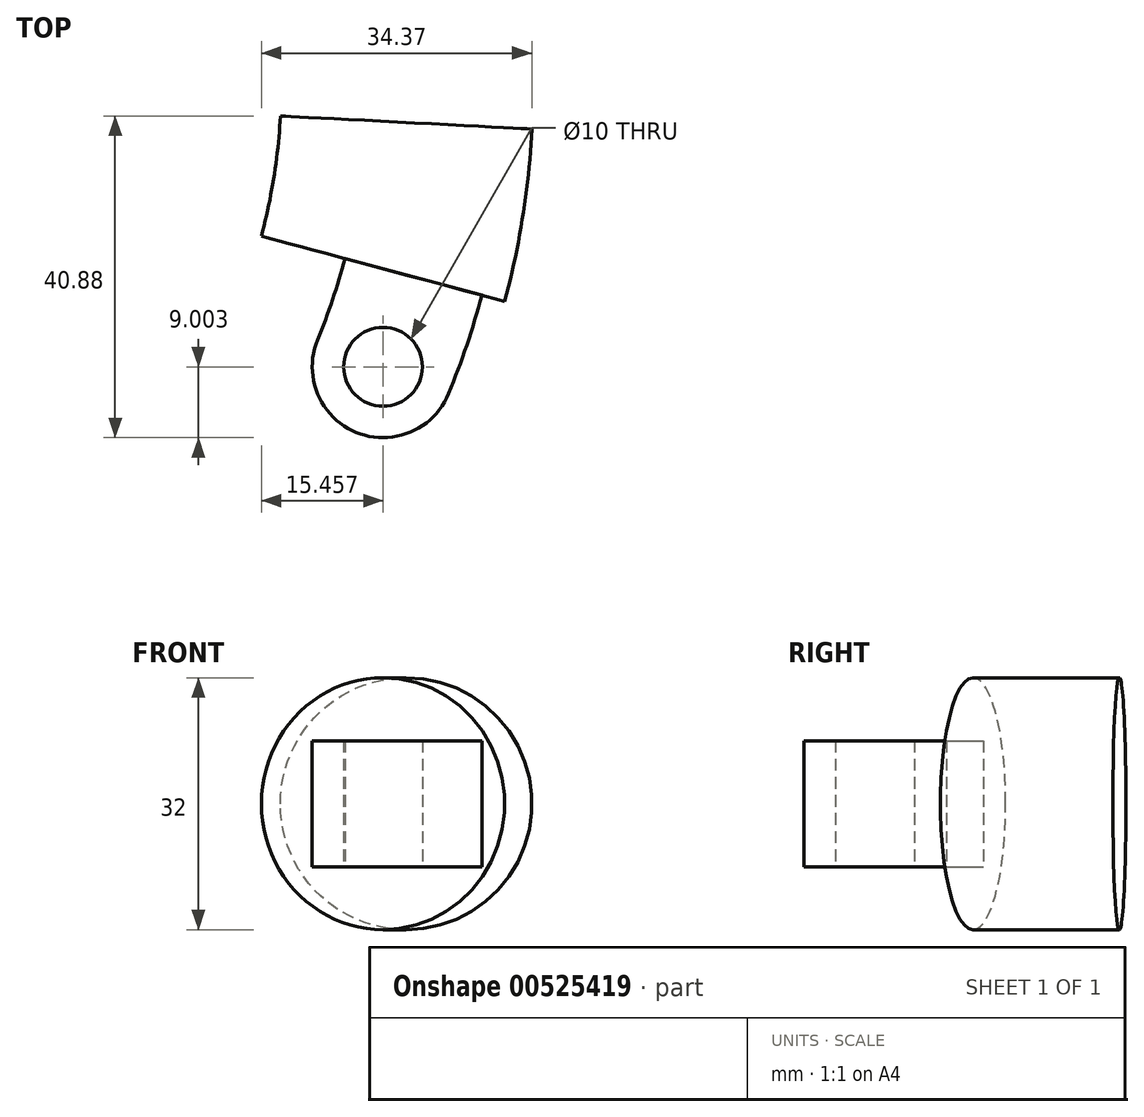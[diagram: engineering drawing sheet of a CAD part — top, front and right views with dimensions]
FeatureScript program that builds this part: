
annotation { "Feature Type Name" : "Feature", "Feature Type Description" : "" }
export const myFeature = defineFeature(function(context is Context, id is Id, definition is map)
    precondition{}
    {
        {
            var Q0;
            Q0=qCreatedBy(makeId("Top.planeOp"),FACE);
            var sketch = newSketch(context, id + "F0", { "sketchPlane" : qUnion([Q0])});
            skCircle(sketch, "E0", {"center": v(0, 0) * mm, "radius": 90 * mm});
            skCircle(sketch, "E1", {"center": v(0, 0) * mm, "radius": 94 * mm});
            skCircle(sketch, "E2", {"center": v(0, 0) * mm, "radius": 120 * mm, "construction": true});
            skCircle(sketch, "E3", {"center": v(0, 0) * mm, "radius": 12.7 * mm});
            skCircle(sketch, "E4", {"center": v(0, 0) * mm, "radius": 25 * mm});
            skLineSegment(sketch, "E5", {"start": v(0, 0) * mm, "end": v(142.42, 0) * mm, "construction": true});
            skLineSegment(sketch, "E6", {"start": v(0, 0) * mm, "end": v(179.75, -9.42) * mm});
            skLineSegment(sketch, "E7", {"start": v(0, 0) * mm, "end": v(124.98, -63.68) * mm, "construction": true});
            skLineSegment(sketch, "E8", {"start": v(0, 0) * mm, "end": v(38.58, -95.5) * mm});
            skLineSegment(sketch, "E9", {"start": v(0, 0) * mm, "end": v(116.18, -75.45) * mm, "construction": true});
            skLineSegment(sketch, "E10", {"start": v(0, 0) * mm, "end": v(86.94, -35.75) * mm, "construction": true});
            skCircle(sketch, "E11", {"center": v(86.94, -35.75) * mm, "radius": 3.5 * mm});
            skCircle(sketch, "E12", {"center": v(86.94, -35.75) * mm, "radius": 5 * mm});
            skCircle(sketch, "E13", {"center": v(86.94, -35.75) * mm, "radius": 9 * mm});
            skArc(sketch, "E14", {"start": v(95.26, -39.17) * mm, "mid": v(100.49, -22.6) * mm, "end": v(102.86, -5.4) * mm});
            skArc(sketch, "E15", {"start": v(78.61, -32.32) * mm, "mid": v(82.93, -18.65) * mm, "end": v(84.88, -4.45) * mm});
            skArc(sketch, "E16", {"start": v(95.26, -39.17) * mm, "mid": v(72.6, -73.06) * mm, "end": v(38.58, -95.5) * mm});
            skPoint(sketch, "E17", {"position": v(89.88, -4.71) * mm});
            skPoint(sketch, "E18", {"position": v(90, 0) * mm});
            skLineSegment(sketch, "E19", {"start": v(20.06, -14.92) * mm, "end": v(67, -52.3) * mm});
            skArc(sketch, "E20", {"start": v(78.61, -32.32) * mm, "mid": v(73.49, -42.71) * mm, "end": v(67, -52.3) * mm});
            skLineSegment(sketch, "E21", {"start": v(0, 0) * mm, "end": v(94.13, -87.78) * mm});
            skLineSegment(sketch, "E22", {"start": v(89.88, -4.71) * mm, "end": v(85.56, -45.75) * mm, "construction": true});
            skLineSegment(sketch, "E23", {"start": v(89.88, -4.71) * mm, "end": v(111, -6.93) * mm, "construction": true});
            skCircle(sketch, "E24", {"center": v(89.88, -4.71) * mm, "radius": 16 * mm, "construction": true});
            skLineSegment(sketch, "E25", {"start": v(0, 0) * mm, "end": v(115.71, -18.33) * mm, "construction": true});
            skLineSegment(sketch, "E26", {"start": v(0, 0) * mm, "end": v(156.61, -16.46) * mm, "construction": true});
            skSolve(sketch);
        }
        {
            var Q0;
            {var subQ5=sQuery(id+"F0.wireOp",EDGE,"E15");Q0=makeQuery(id+"F0.imprint","IMPRINT",FACE,{"disambiguationData":[TD([[makeQuery(id+"F0.imprint","IMPRINT",EDGE,{"derivedFrom":subQ5}),-1.0]])]});}
            var Q1;
            {var subQ0=sQuery(id+"F0.wireOp",EDGE,"E13");var subQ2=sQuery(id+"F0.wireOp",EDGE,"E0");var subQ7=makeQuery(id+"F0.imprint","INTERSECT",VERTEX,{"disambiguationData":[OD(0.0)],"derivedFrom":[subQ2,subQ0]});Q1=makeQuery(id+"F0.imprint","IMPRINT",FACE,{"disambiguationData":[TD([[makeQuery(id+"F0.imprint","IMPRINT",EDGE,{"disambiguationData":[TD([[subQ7,-1.0]])],"derivedFrom":subQ2}),1.0]])]});}
            var Q2;
            {var subQ0=sQuery(id+"F0.wireOp",EDGE,"E13");var subQ1=sQuery(id+"F0.wireOp",EDGE,"E0");var subQ2=makeQuery(id+"F0.imprint","INTERSECT",VERTEX,{"disambiguationData":[OD(0.0)],"derivedFrom":[subQ1,subQ0]});Q2=makeQuery(id+"F0.imprint","IMPRINT",FACE,{"disambiguationData":[TD([[makeQuery(id+"F0.imprint","IMPRINT",EDGE,{"disambiguationData":[TD([[subQ2,-1.0]])],"derivedFrom":subQ1}),-1.0]])]});}
            var Q3;
            {var subQ1=sQuery(id+"F0.wireOp",EDGE,"E1");var subQ3=sQuery(id+"F0.wireOp",EDGE,"E13");var subQ6=makeQuery(id+"F0.imprint","INTERSECT",VERTEX,{"disambiguationData":[OD(0.0)],"derivedFrom":[subQ1,subQ3]});Q3=makeQuery(id+"F0.imprint","IMPRINT",FACE,{"disambiguationData":[TD([[makeQuery(id+"F0.imprint","IMPRINT",EDGE,{"disambiguationData":[TD([[subQ6,-1.0]])],"derivedFrom":subQ1}),-1.0]])]});}
            var Q4;
            {var subQ0=sQuery(id+"F0.wireOp",EDGE,"E12");var subQ1=sQuery(id+"F0.wireOp",EDGE,"E0");var subQ2=makeQuery(id+"F0.imprint","INTERSECT",VERTEX,{"disambiguationData":[OD(1.0)],"derivedFrom":[subQ1,subQ0]});Q4=makeQuery(id+"F0.imprint","IMPRINT",FACE,{"disambiguationData":[TD([[makeQuery(id+"F0.imprint","IMPRINT",EDGE,{"disambiguationData":[TD([[subQ2,-1.0]])],"derivedFrom":subQ1}),-1.0]])]});}
            var Q5;
            {var subQ0=sQuery(id+"F0.wireOp",EDGE,"E13");var subQ1=sQuery(id+"F0.wireOp",EDGE,"E0");var subQ2=makeQuery(id+"F0.imprint","INTERSECT",VERTEX,{"disambiguationData":[OD(1.0)],"derivedFrom":[subQ1,subQ0]});Q5=makeQuery(id+"F0.imprint","IMPRINT",FACE,{"disambiguationData":[TD([[makeQuery(id+"F0.imprint","IMPRINT",EDGE,{"disambiguationData":[TD([[subQ2,-1.0]])],"derivedFrom":subQ1}),-1.0]])]});}
            var Q6;
            {var subQ5=sQuery(id+"F0.wireOp",EDGE,"E14");Q6=makeQuery(id+"F0.imprint","IMPRINT",FACE,{"disambiguationData":[TD([[makeQuery(id+"F0.imprint","IMPRINT",EDGE,{"derivedFrom":subQ5}),1.0]])]});}
            extrude(context, id + "F1", {"entities" : qUnion([Q0, Q1, Q2, Q3, Q4, Q5, Q6]), "endBound" : BoundingType.SYMMETRIC, "depth" : 16 * mm, "offsetDistance" : 25 * mm});
        }
        {
            var Q0;
            Q0=makeQuery(id+"F1.opExtrude","SWEPT_FACE",FACE,{"disambiguationData":[OSD([sQuery(id+"F0.wireOp",EDGE,"E6")])]});
            cPlane(context, id + "F2", {"entities" : qUnion([Q0]), "cplaneType" : CPlaneType.OFFSET, "offset" : 0 * mm, "width" : 150 * mm, "height" : 150 * mm});
        }
        {
            var Q0;
            Q0=qCreatedBy(id+"F2.planeOp",FACE);
            var sketch = newSketch(context, id + "F3", { "sketchPlane" : qUnion([Q0])});
            skCircle(sketch, "E27", {"center": v(-90, 0) * mm, "radius": 16 * mm});
            skLineSegment(sketch, "E28", {"start": v(0, 0) * mm, "end": v(0, 33.3) * mm, "construction": true});
            skSolve(sketch);
        }
        {
            var Q0;
            Q0=makeQuery(id+"F3.imprint","IMPRINT",FACE,{"disambiguationData":[TD([[makeQuery(id+"F3.imprint","IMPRINT",EDGE,{"derivedFrom":sQuery(id+"F3.wireOp",EDGE,"E27")}),1.0]])]});
            var Q1;
            Q1=sQuery(id+"F3.wireOp",EDGE,"E28");
            revolve(context, id + "F4", {"operationType" : NewBodyOperationType.ADD, "entities" : qUnion([Q0]), "axis" : qUnion([Q1]), "revolveType" : RevolveType.ONE_DIRECTION, "oppositeDirection" : true, "angle" : 12 * degree});
        }
    });
